# Revit family: Shower_Trim-DXV-Percy-D351055X0_Series
name_source: partatom
category: Plumbing Fixtures
revit_build: Autodesk Revit 2014 (Build: 20130308_1515(x64)
units: mm (PartAtom-declared; Revit-internal decimal feet)

## types (10) — shared parameters
Assembly Code = D2010710
CW Connection = Yes
CWFU = 3
Cold Water Connection Diameter = 1/2"
Cold Water Connection Radius = 1/4"
Default Elevation = 44"
Description = Percy Pressure Balance Shower Valve Trim
HW Connection = Yes
HWFU = 3
Height = 7 5/16"
Hot Water Connection Diameter = 1"
Hot Water Connection Radius = 1/4"
Installation Type = Wall Mounted
Length = 3"
Manufacturer = DXV
Price = Prices may vary. Please consult Manufacturer Representative for most up-to-date price list.
Product Documentation Link = https://dxv01.blob.core.windows.net
Product Page URL = https://www.dxv.com
Tempered Water Connection Diameter = 1/2"
Tempered Water Connection Radius = 1/4"
Tub Plug = Yes
Tub Port Connection Diameter = 0"
Tub Port Connection Radius = 0"
URL = www.dxv.com
Vent Connection = No
WFU = 4
Warranty Documentation Link = https://www.dxv.com
Waste Connection = No
Width = 7 5/16"

## per-type parameters (varying)
| type | ADA Compliant | Cross Handle Option | Finish | Lever Handle Option | Material | Model | Tri-Spoke Handle Option |
| D35105540.144 | No | Yes | Cast Brass-DXV-144-Brushed Nickel | No | Cast Brass-DXV-144-Brushed Nickel | D35105540.144 | No |
| D35105540.100 | No | Yes | Cast Brass-DXV-100-Polished Chrome | No | Cast Brass-DXV-100-Polished Chrome | D35105540.100 | No |
| D35105500.100 | Yes | No | Cast Brass-DXV-100-Polished Chrome | Yes | Cast Brass-DXV-100-Polished Chrome | D35105500.100 | No |
| D35105500.144 | Yes | No | Cast Brass-DXV-144-Brushed Nickel | Yes | Cast Brass-DXV-144-Brushed Nickel | D35105500.144 | No |
| D35105570.100 | Yes | No | Cast Brass-DXV-100-Polished Chrome | No | Cast Brass-DXV-100-Polished Chrome | D35105570.100 | Yes |
| D35105570.144 | Yes | No | Cast Brass-DXV-144-Brushed Nickel | No | Cast Brass-DXV-144-Brushed Nickel | D35105570.144 | Yes |
| D35105540RB.100 | No | Yes | Cast Brass-DXV-100-Polished Chrome | No | Cast Brass-DXV-100-Polished Chrome | D35105540RB.100 | No |
| D35105540RB.144 | No | Yes | Cast Brass-DXV-144-Brushed Nickel | No | Cast Brass-DXV-144-Brushed Nickel | D35105540RB.144 | No |
| D35105500RB.100 | Yes | No | Cast Brass-DXV-100-Polished Chrome | Yes | Cast Brass-DXV-100-Polished Chrome | D35105500.100 | No |
| D35105500RB.144 | Yes | No | Cast Brass-DXV-144-Brushed Nickel | Yes | Cast Brass-DXV-144-Brushed Nickel | D35105500RB.144 | No |

## geometry (parser evidence)
native form markers: Sweep x3
no freeform markers — native parametric forms only
